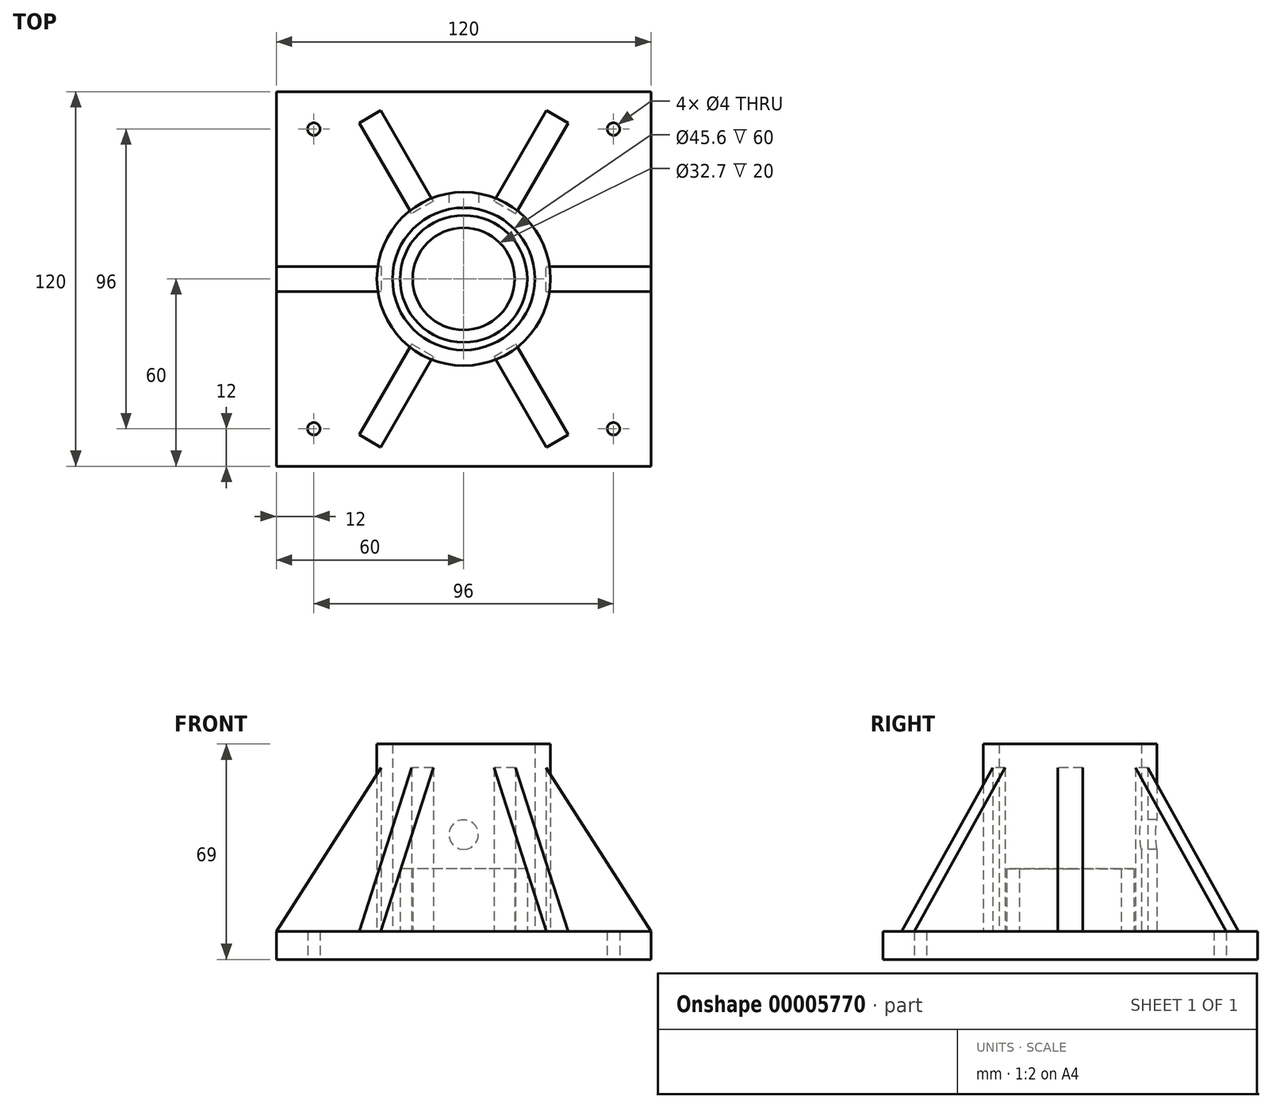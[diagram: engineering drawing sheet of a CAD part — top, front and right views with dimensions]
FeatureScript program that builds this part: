
annotation { "Feature Type Name" : "Feature", "Feature Type Description" : "" }
export const myFeature = defineFeature(function(context is Context, id is Id, definition is map)
    precondition{}
    {
        {
            var Q0;
            Q0=qCreatedBy(makeId("Top.planeOp"),FACE);
            var sketch = newSketch(context, id + "F0", { "sketchPlane" : qUnion([Q0])});
            skLineSegment(sketch, "E0.rect.bottom", {"start": v(-60, 60) * mm, "end": v(60, 60) * mm});
            skLineSegment(sketch, "E0.rect.top", {"start": v(-60, -60) * mm, "end": v(60, -60) * mm});
            skLineSegment(sketch, "E0.rect.left", {"start": v(-60, 60) * mm, "end": v(-60, -60) * mm});
            skLineSegment(sketch, "E0.rect.right", {"start": v(60, 60) * mm, "end": v(60, -60) * mm});
            skPoint(sketch, "E0.rect.middle", {"position": v(0, 0) * mm});
            skLineSegment(sketch, "E1", {"start": v(0, -60) * mm, "end": v(0, 60) * mm, "construction": true});
            skLineSegment(sketch, "E2", {"start": v(60, 0) * mm, "end": v(-60, 0) * mm, "construction": true});
            skCircle(sketch, "E3", {"center": v(48, 48) * mm, "radius": 2 * mm});
            skCircle(sketch, "E4.0.MirrorC", {"center": v(48, -48) * mm, "radius": 2 * mm});
            skCircle(sketch, "E5.0.MirrorC", {"center": v(-48, -48) * mm, "radius": 2 * mm});
            skCircle(sketch, "E5.1.MirrorC", {"center": v(-48, 48) * mm, "radius": 2 * mm});
            skSolve(sketch);
        }
        {
            var Q0;
            Q0 = qSketchRegion(id + "F0", true);
            extrude(context, id + "F1", {"entities" : qUnion([Q0]), "depth" : 9 * mm});
        }
        {
            var Q0;
            Q0=makeQuery(id+"F1.opExtrude","CAP_FACE",FACE,{"disambiguationData":[OSD([sQuery(id+"F0.wireOp",EDGE,"E0.rect.bottom"),sQuery(id+"F0.wireOp",EDGE,"E0.rect.top"),sQuery(id+"F0.wireOp",EDGE,"E0.rect.left"),sQuery(id+"F0.wireOp",EDGE,"E0.rect.right")])],"isStart":false});
            var sketch = newSketch(context, id + "F2", { "sketchPlane" : qUnion([Q0])});
            skCircle(sketch, "E6", {"center": v(0, 0) * mm, "radius": 27.8 * mm});
            skCircle(sketch, "E7", {"center": v(0, 0) * mm, "radius": 22.8 * mm});
            skCircle(sketch, "E8", {"center": v(0, 0) * mm, "radius": 20.35 * mm});
            skCircle(sketch, "E9", {"center": v(0, 0) * mm, "radius": 16.35 * mm});
            skSolve(sketch);
        }
        {
            var Q0;
            Q0 = qSketchRegion(id + "F2", true);
            extrude(context, id + "F3", {"entities" : qUnion([Q0]), "operationType" : NewBodyOperationType.ADD, "depth" : 60 * mm});
        }
        {
            var Q0;
            Q0=makeQuery(id+"F2.imprint","IMPRINT",FACE,{"disambiguationData":[TD([[makeQuery(id+"F2.imprint","IMPRINT",EDGE,{"derivedFrom":sQuery(id+"F2.wireOp",EDGE,"E8")}),1.0]])]});
            extrude(context, id + "F4", {"entities" : qUnion([Q0]), "operationType" : NewBodyOperationType.ADD, "depth" : 20 * mm});
        }
        {
            var Q0;
            Q0=qCreatedBy(makeId("Front.planeOp"),FACE);
            var sketch = newSketch(context, id + "F5", { "sketchPlane" : qUnion([Q0])});
            skLineSegment(sketch, "E10", {"start": v(26.4, 61.45) * mm, "end": v(60, 9) * mm});
            skLineSegment(sketch, "E11.0", {"start": v(-60, 9) * mm, "end": v(60, 9) * mm});
            skLineSegment(sketch, "E12", {"start": v(26.4, 61.45) * mm, "end": v(26.4, 9) * mm});
            skLineSegment(sketch, "E13", {"start": v(26.4, 9) * mm, "end": v(60, 9) * mm});
            skSolve(sketch);
        }
        {
            var Q0;
            Q0 = qSketchRegion(id + "F5", true);
            extrude(context, id + "F6", {"entities" : qUnion([Q0]), "endBound" : BoundingType.SYMMETRIC, "depth" : 8 * mm});
        }
        {
            var Q0;
            Q0=makeQuery(id+"F6.opExtrude","SWEPT_BODY",BODY,{"disambiguationData":[OSD([sQuery(id+"F5.wireOp",EDGE,"E10"),sQuery(id+"F5.wireOp",EDGE,"E12"),sQuery(id+"F5.wireOp",EDGE,"E13")])]});
            var Q1;
            Q1=makeQuery(id+"F3.opExtrude","CAP_EDGE",EDGE,{"disambiguationData":[OSD([sQuery(id+"F2.wireOp",EDGE,"E7")])],"isStart":false});
            circularPattern(context, id + "F7", {"entities" : qUnion([Q0]), "axis" : qUnion([Q1]), "angle" : 360 * degree, "instanceCount" : 6, "equalSpace" : true});
        }
        {
            var Q0;
            Q0=qCreatedBy(makeId("Front.planeOp"),FACE);
            var sketch = newSketch(context, id + "F8", { "sketchPlane" : qUnion([Q0])});
            skCircle(sketch, "E14", {"center": v(0, 40) * mm, "radius": 4.75 * mm});
            skSolve(sketch);
        }
        {
            var Q0;
            Q0=makeQuery(id+"F8.imprint","IMPRINT",FACE,{"disambiguationData":[TD([[makeQuery(id+"F8.imprint","IMPRINT",EDGE,{"derivedFrom":sQuery(id+"F8.wireOp",EDGE,"E14")}),1.0]])]});
            extrude(context, id + "F9", {"entities" : qUnion([Q0]), "operationType" : NewBodyOperationType.REMOVE, "oppositeDirection" : true, "depth" : 60 * mm});
        }
    });
